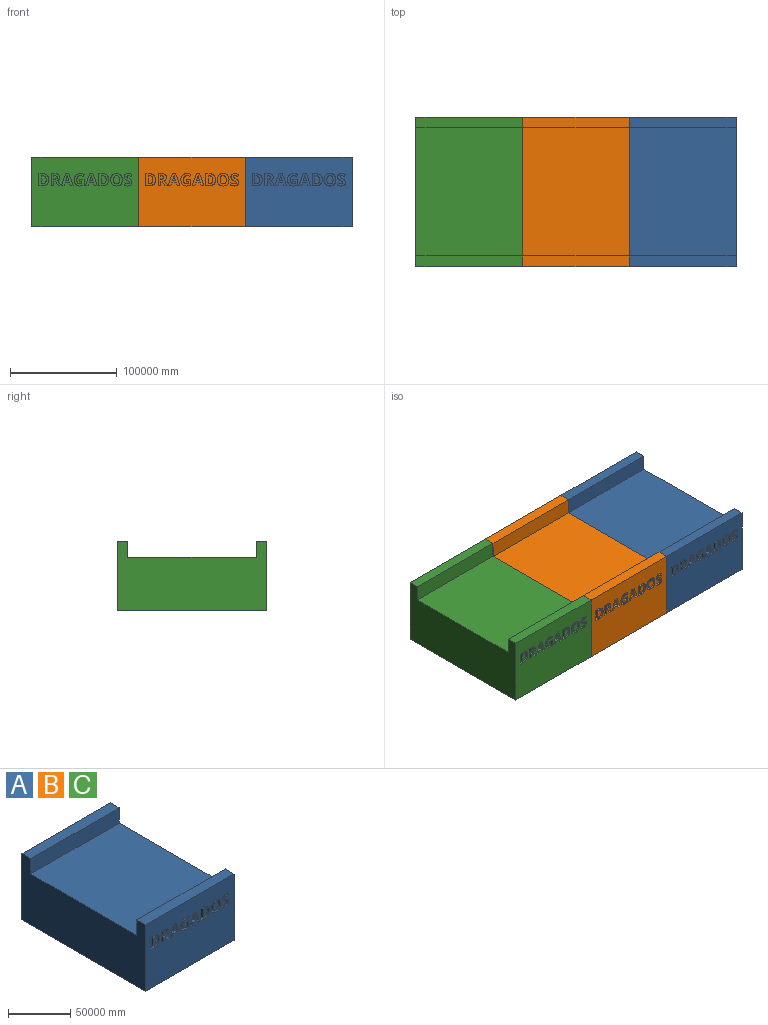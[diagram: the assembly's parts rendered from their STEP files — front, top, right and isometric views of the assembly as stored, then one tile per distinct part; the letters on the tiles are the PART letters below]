
ASSEMBLY  parts=3 mates=2
PART A: 152 faces, bbox 100000x140000x65000 mm
  f0: plane 100000x65000mm, normal (0,-1,0), area 5889989465.6mm2, adj f2,f3,f4,f9,f10,f11,f12,f13
  f1: plane 120000x100000mm, normal (0,0,1), area 12000000000mm2, adj f2,f4,f6,f8
  f2: plane 140000x65000mm, normal (-1,0,0), area 7300000000mm2, adj f0,f1,f3,f5,f6,f7,f8,f9
  f3: plane 140000x100000mm, normal (0,0,-1), area 14000000000mm2, adj f0,f2,f4,f5
  f4: plane 140000x65000mm, normal (1,0,0), area 7300000000mm2, adj f0,f1,f3,f5,f6,f7,f8,f9
  f5: plane 100000x65000mm, normal (0,1,0), area 6500000000mm2, adj f2,f3,f4,f7
  f6: plane 100000x15000mm, normal (0,-1,0), area 1500000000mm2, adj f1,f2,f4,f7
  f7: plane 100000x10000mm, normal (0,0,1), area 1000000000mm2, adj f2,f4,f5,f6
  f8: plane 100000x15000mm, normal (0,1,0), area 1500000000mm2, adj f1,f2,f4,f9
  f9: plane 100000x10000mm, normal (0,0,1), area 1000000000mm2, adj f0,f2,f4,f8
  f10: plane 4511.8x3000mm, normal (0,0,-1), area 13535406.6mm2, adj f0,f11,f28,f29
  f11: plane 3000x2008.29mm, normal (1,0,0), area 6024861.1mm2, adj f0,f10,f12,f29
  f12: plane 3000x2155.11mm, normal (0,0,1), area 6465340.4mm2, adj f0,f11,f13,f29
  f13: plane 3000x2371.62mm, normal (1,0,0), area 7114860.7mm2, adj f0,f12,f14,f29
  f14: extruded ~3000x1532.97mm, area 4629580.4mm2, adj f0,f13,f15,f29
  f15: extruded ~3000x2203.64mm, area 7506016mm2, adj f0,f14,f16,f29
  f16: extruded ~3000x2827.03mm, area 8939362.1mm2, adj f0,f15,f17,f29
  f17: extruded ~3000x2822.05mm, area 9132796.1mm2, adj f0,f16,f18,f29
  f18: extruded ~3000x2503.52mm, area 8406838mm2, adj f0,f17,f19,f29
  f19: extruded ~3000x2590.62mm, area 8066421.4mm2, adj f0,f18,f20,f29
  f20: plane 3000x1928.65mm, normal (-0.92,0,0.38), area 6265491.2mm2, adj f0,f19,f21,f29
  f21: extruded ~3377.01x3000mm, area 10418684.1mm2, adj f0,f20,f22,f29
  f22: extruded ~4364.98x3000mm, area 14252224.5mm2, adj f0,f21,f23,f29
  f23: extruded ~4291.56x3000mm, area 14101973.1mm2, adj f0,f22,f24,f29
  f24: extruded ~4345.07x3000mm, area 13969649.8mm2, adj f0,f23,f25,f29
  f25: extruded ~3930.72x3000mm, area 13034389.8mm2, adj f0,f24,f26,f29
  f26: extruded ~3000x1978.42mm, area 5956492.1mm2, adj f0,f25,f27,f29
  f27: extruded ~3000x2065.52mm, area 6384867.5mm2, adj f0,f26,f28,f29
  f28: plane 5895.45x3000mm, normal (-1,0,0), area 17686364.2mm2, adj f0,f10,f27,f29
  f29: plane 11688.88x9332.19mm, normal (0,-1,0), area 62986172mm2, adj f10,f11,f12,f13,f14,f15,f16,f17
  f30: extruded ~3000x2870.58mm, area 9030077.2mm2, adj f31,f43,f44,f147
  f31: extruded ~3000x2871.83mm, area 9041235.7mm2, adj f30,f32,f44,f147
  f32: extruded ~3000x2168.8mm, area 7406378.6mm2, adj f31,f33,f44,f147
  f33: extruded ~3839.88x3000mm, area 16403148.1mm2, adj f32,f34,f44,f147
  f34: extruded ~3834.91x3000mm, area 16424551mm2, adj f33,f43,f44,f147
  f35: extruded ~4341.33x3000mm, area 14012505mm2, adj f0,f36,f42,f44
  f36: extruded ~4338.85x3000mm, area 13992602.8mm2, adj f0,f35,f37,f44
  f37: extruded ~4009.11x3000mm, area 13243213.6mm2, adj f0,f36,f38,f44
  f38: extruded ~4024.04x3000mm, area 13263273.8mm2, adj f0,f37,f39,f44
  f39: extruded ~4336.36x3000mm, area 14008077.7mm2, adj f0,f38,f40,f44
  f40: extruded ~4356.27x3000mm, area 14055744mm2, adj f0,f39,f41,f44
  f41: extruded ~4012.84x3000mm, area 13261248.6mm2, adj f0,f40,f42,f44
  f42: extruded ~4012.84x3000mm, area 13261248.6mm2, adj f0,f35,f41,f44
  f43: extruded ~3000x2161.34mm, area 7382216.9mm2, adj f30,f34,f44,f147
  f44: plane 11706.3x10825.34mm, normal (0,-1,0), area 67703911.6mm2, adj f30,f31,f32,f33,f34,f35,f36,f37
  f45: extruded ~3663.2x3235.16mm, area 16809076.1mm2, adj f46,f56,f57,f148
  f46: extruded ~3740.34x3484.02mm, area 17594489.8mm2, adj f45,f47,f57,f148
  f47: plane 3000x1032.76mm, normal (0,0,-1), area 3098286.7mm2, adj f46,f48,f57,f148
  f48: plane 7403.54x3000mm, normal (-1,0,0), area 22210609.3mm2, adj f47,f56,f57,f148
  f49: extruded ~4300.27x3000mm, area 14174793.3mm2, adj f0,f50,f55,f57
  f50: extruded ~4107.41x3000mm, area 13544800.3mm2, adj f0,f49,f51,f57
  f51: extruded ~4325.16x3000mm, area 14051984.7mm2, adj f0,f50,f52,f57
  f52: plane 3568.63x3000mm, normal (0,0,-1), area 10705887mm2, adj f0,f51,f53,f57
  f53: plane 11370.34x3000mm, normal (1,0,0), area 34111016.4mm2, adj f0,f52,f54,f57
  f54: plane 3220.23x3000mm, normal (0,0,1), area 9660681.8mm2, adj f0,f53,f55,f57
  f55: extruded ~4615.08x3000mm, area 14906133.2mm2, adj f0,f49,f54,f57
  f56: plane 3000x1281.62mm, normal (0,0,1), area 3844861.8mm2, adj f45,f48,f57,f148
  f57: plane 11370.34x9434.22mm, normal (0,-1,0), area 65817079.6mm2, adj f45,f46,f47,f48,f49,f50,f51,f52
  f58: extruded ~4160.91x3000mm, area 13065876.7mm2, adj f59,f69,f70,f149
  f59: plane 3000x2961.41mm, normal (0,0,-1), area 8884243.7mm2, adj f58,f60,f70,f149
  f60: extruded ~4922.42x3000mm, area 15410954.9mm2, adj f59,f69,f70,f149
  f61: plane 3000x2707.58mm, normal (0.96,0,0.29), area 8490318.5mm2, adj f0,f62,f68,f70
  f62: plane 3000x2598.08mm, normal (0,0,1), area 7794244.1mm2, adj f0,f61,f63,f70
  f63: plane 11417.62x4029.02mm, normal (-0.94,0,-0.33), area 36322935mm2, adj f0,f62,f64,f70
  f64: plane 3000x2946.48mm, normal (0,0,-1), area 8839449.2mm2, adj f0,f63,f65,f70
  f65: plane 11417.62x4014.09mm, normal (0.94,0,-0.33), area 36308053.4mm2, adj f0,f64,f66,f70
  f66: plane 3000x2598.08mm, normal (0,0,1), area 7794244.1mm2, adj f0,f65,f67,f70
  f67: plane 3000x2707.58mm, normal (-0.96,0,0.29), area 8490318.5mm2, adj f0,f66,f68,f70
  f68: plane 4145.98x3000mm, normal (0,0,1), area 12437941.2mm2, adj f0,f61,f67,f70
  f69: extruded ~3000x761.51mm, area 2367510.5mm2, adj f58,f60,f70,f149
  f70: plane 11417.62x10989.59mm, normal (0,-1,0), area 58950877mm2, adj f58,f59,f60,f61,f62,f63,f64,f65
  f71: extruded ~3000x2427.61mm, area 8303820.4mm2, adj f0,f72,f98,f99
  f72: extruded ~3000x1877.64mm, area 6017220.3mm2, adj f0,f71,f73,f99
  f73: extruded ~3000x2186.22mm, area 8069418.4mm2, adj f0,f72,f74,f99
  f74: extruded ~3000x1526.75mm, area 5169060.9mm2, adj f0,f73,f75,f99
  f75: extruded ~3000x470.34mm, area 1985542.8mm2, adj f0,f74,f76,f99
  f76: extruded ~3000x556.2mm, area 1749833.2mm2, adj f0,f75,f77,f99
  f77: extruded ~3000x831.19mm, area 2815640.2mm2, adj f0,f76,f78,f99
  f78: extruded ~3000x1050.18mm, area 3364291mm2, adj f0,f77,f79,f99
  f79: extruded ~3000x1169.63mm, area 3545737.4mm2, adj f0,f78,f80,f99
  f80: extruded ~3000x1505.59mm, area 4783799.7mm2, adj f0,f79,f81,f99
  f81: plane 3000x1876.39mm, normal (-0.92,0,0.38), area 6092071.1mm2, adj f0,f80,f82,f99
  f82: extruded ~3000x1683.53mm, area 5356881.6mm2, adj f0,f81,f83,f99
  f83: extruded ~3000x1690.99mm, area 5125435.5mm2, adj f0,f82,f84,f99
  f84: extruded ~3000x2827.03mm, area 9053745.9mm2, adj f0,f83,f85,f99
  f85: extruded ~3000x2372.86mm, area 8020942mm2, adj f0,f84,f86,f99
  f86: extruded ~3000x1398.58mm, area 4340097.6mm2, adj f0,f85,f87,f99
  f87: extruded ~3000x1050.18mm, area 4044865.9mm2, adj f0,f86,f88,f99
  f88: extruded ~3000x1561.59mm, area 5484625.9mm2, adj f0,f87,f89,f99
  f89: extruded ~3000x1474.49mm, area 4993462.5mm2, adj f0,f88,f90,f99
  f90: extruded ~3000x548.73mm, area 2242214.9mm2, adj f0,f89,f91,f99
  f91: extruded ~3000x594.77mm, area 1901623.8mm2, adj f0,f90,f92,f99
  f92: extruded ~3000x902.11mm, area 3117233.3mm2, adj f0,f91,f93,f99
  f93: extruded ~3000x1215.67mm, area 3817270.7mm2, adj f0,f92,f94,f99
  f94: extruded ~3000x1459.55mm, area 4435350.4mm2, adj f0,f93,f95,f99
  f95: extruded ~3000x1947.32mm, area 6239494.7mm2, adj f0,f94,f96,f99
  f96: plane 3000x2239.73mm, normal (1,0,0), area 6719175.9mm2, adj f0,f95,f97,f99
  f97: extruded ~3220.23x3000mm, area 9965344.2mm2, adj f0,f96,f98,f99
  f98: extruded ~3082.11x3000mm, area 9807859.6mm2, adj f0,f71,f97,f99
  f99: plane 11688.88x7411mm, normal (0,-1,0), area 48752152.3mm2, adj f71,f72,f73,f74,f75,f76,f77,f78
  f100: extruded ~3663.2x3235.16mm, area 16809076.1mm2, adj f101,f111,f112,f150
  f101: extruded ~3740.34x3484.02mm, area 17594489.8mm2, adj f100,f102,f112,f150
  f102: plane 3000x1032.76mm, normal (0,0,-1), area 3098286.7mm2, adj f101,f103,f112,f150
  f103: plane 7403.54x3000mm, normal (-1,0,0), area 22210609.3mm2, adj f102,f111,f112,f150
  f104: extruded ~4300.27x3000mm, area 14174793.3mm2, adj f0,f105,f110,f112
  f105: extruded ~4107.41x3000mm, area 13544800.3mm2, adj f0,f104,f106,f112
  f106: extruded ~4325.16x3000mm, area 14051984.7mm2, adj f0,f105,f107,f112
  f107: plane 3568.63x3000mm, normal (0,0,-1), area 10705887mm2, adj f0,f106,f108,f112
  f108: plane 11370.34x3000mm, normal (1,0,0), area 34111016.4mm2, adj f0,f107,f109,f112
  f109: plane 3220.23x3000mm, normal (0,0,1), area 9660681.8mm2, adj f0,f108,f110,f112
  f110: extruded ~4615.08x3000mm, area 14906133.2mm2, adj f0,f104,f109,f112
  f111: plane 3000x1281.62mm, normal (0,0,1), area 3844861.8mm2, adj f100,f103,f112,f150
  f112: plane 11370.34x9434.22mm, normal (0,-1,0), area 65817079.6mm2, adj f100,f101,f102,f103,f104,f105,f106,f107
  f113: plane 4362.49x3000mm, normal (-1,0,0), area 13087461.5mm2, adj f0,f114,f131,f132
  f114: plane 3000x1281.62mm, normal (0,0,1), area 3844861.8mm2, adj f0,f113,f115,f132
  f115: plane 4362.49x3000mm, normal (0.85,0,0.53), area 15415085.6mm2, adj f0,f114,f116,f132
  f116: plane 3000x2675.23mm, normal (0,0,1), area 8025682.3mm2, adj f0,f115,f117,f132
  f117: extruded ~4954.77x3344.66mm, area 17934115.7mm2, adj f0,f116,f118,f132
  f118: extruded ~3000x1564.08mm, area 6034781mm2, adj f0,f117,f119,f132
  f119: extruded ~3000x1784.31mm, area 5695065.4mm2, adj f0,f118,f120,f132
  f120: extruded ~3000x2563.24mm, area 8707609.6mm2, adj f0,f119,f121,f132
  f121: extruded ~3430.51x3000mm, area 10776834.6mm2, adj f0,f120,f122,f132
  f122: plane 3312.31x3000mm, normal (0,0,-1), area 9936914.6mm2, adj f0,f121,f123,f132
  f123: plane 11370.34x3000mm, normal (1,0,0), area 34111016.4mm2, adj f0,f122,f131,f132
  f124: plane 3000x776.44mm, normal (0,0,-1), area 2329314.3mm2, adj f125,f130,f132,f133
  f125: plane 3070.91x3000mm, normal (-1,0,0), area 9212736.7mm2, adj f124,f126,f132,f133
  f126: plane 3000x731.64mm, normal (0,0,1), area 2194930.8mm2, adj f125,f127,f132,f133
  f127: extruded ~3000x1720.86mm, area 5325056.4mm2, adj f126,f128,f132,f133
  f128: extruded ~3000x1150.97mm, area 4022426.4mm2, adj f127,f129,f132,f133
  f129: extruded ~3000x1197.01mm, area 4112647.7mm2, adj f128,f130,f132,f133
  f130: extruded ~3000x1688.5mm, area 5268649.4mm2, adj f124,f129,f132,f133
  f131: plane 3000x2411.44mm, normal (0,0,1), area 7234312.7mm2, adj f0,f113,f123,f132
  f132: plane 11370.34x9083.33mm, normal (0,-1,0), area 63126842mm2, adj f113,f114,f115,f116,f117,f118,f119,f120
  f133: plane 3070.91x3008.7mm, normal (0,-1,0), area 8156719.4mm2, adj f124,f125,f126,f127,f128,f129,f130
  f134: extruded ~4160.91x3000mm, area 13065876.7mm2, adj f135,f145,f146,f151
  f135: plane 3000x2961.41mm, normal (0,0,-1), area 8884243.7mm2, adj f134,f136,f146,f151
  f136: extruded ~4922.42x3000mm, area 15410954.9mm2, adj f135,f145,f146,f151
  f137: plane 3000x2707.58mm, normal (0.96,0,0.29), area 8490318.5mm2, adj f0,f138,f144,f146
  f138: plane 3000x2598.08mm, normal (0,0,1), area 7794244.1mm2, adj f0,f137,f139,f146
  f139: plane 11417.62x4029.02mm, normal (-0.94,0,-0.33), area 36322935mm2, adj f0,f138,f140,f146
  f140: plane 3000x2946.48mm, normal (0,0,-1), area 8839449.2mm2, adj f0,f139,f141,f146
  f141: plane 11417.62x4014.09mm, normal (0.94,0,-0.33), area 36308053.4mm2, adj f0,f140,f142,f146
  f142: plane 3000x2598.08mm, normal (0,0,1), area 7794244.1mm2, adj f0,f141,f143,f146
  f143: plane 3000x2707.58mm, normal (-0.96,0,0.29), area 8490318.5mm2, adj f0,f142,f144,f146
  f144: plane 4145.98x3000mm, normal (0,0,1), area 12437941.2mm2, adj f0,f137,f143,f146
  f145: extruded ~3000x761.51mm, area 2367510.5mm2, adj f134,f136,f146,f151
  f146: plane 11417.62x10989.59mm, normal (0,-1,0), area 58950877mm2, adj f134,f135,f136,f137,f138,f139,f140,f141
  f147: plane 7674.79x5768.54mm, normal (0,-1,0), area 36859398.6mm2, adj f30,f31,f32,f33,f34,f43
  f148: plane 7403.54x4516.78mm, normal (0,-1,0), area 29293068.7mm2, adj f45,f46,f47,f48,f56
  f149: plane 4922.42x2961.41mm, normal (0,-1,0), area 7151643.9mm2, adj f58,f59,f60,f69
  f150: plane 7403.54x4516.78mm, normal (0,-1,0), area 29293068.7mm2, adj f100,f101,f102,f103,f111
  f151: plane 4922.42x2961.41mm, normal (0,-1,0), area 7151643.9mm2, adj f134,f135,f136,f145
PART B: same geometry as A
PART C: same geometry as A
PLACE A t=(200000,0,0)mm
PLACE B t=(100000,0,0)mm
PLACE C at identity fixed
MATE fastened C.f4 <-> B.f2  axis (1,0,0) through (95000.32,0,24240)mm
MATE fastened B.f4 <-> A.f2  axis (1,0,0) through (195000.32,0,24240)mm
